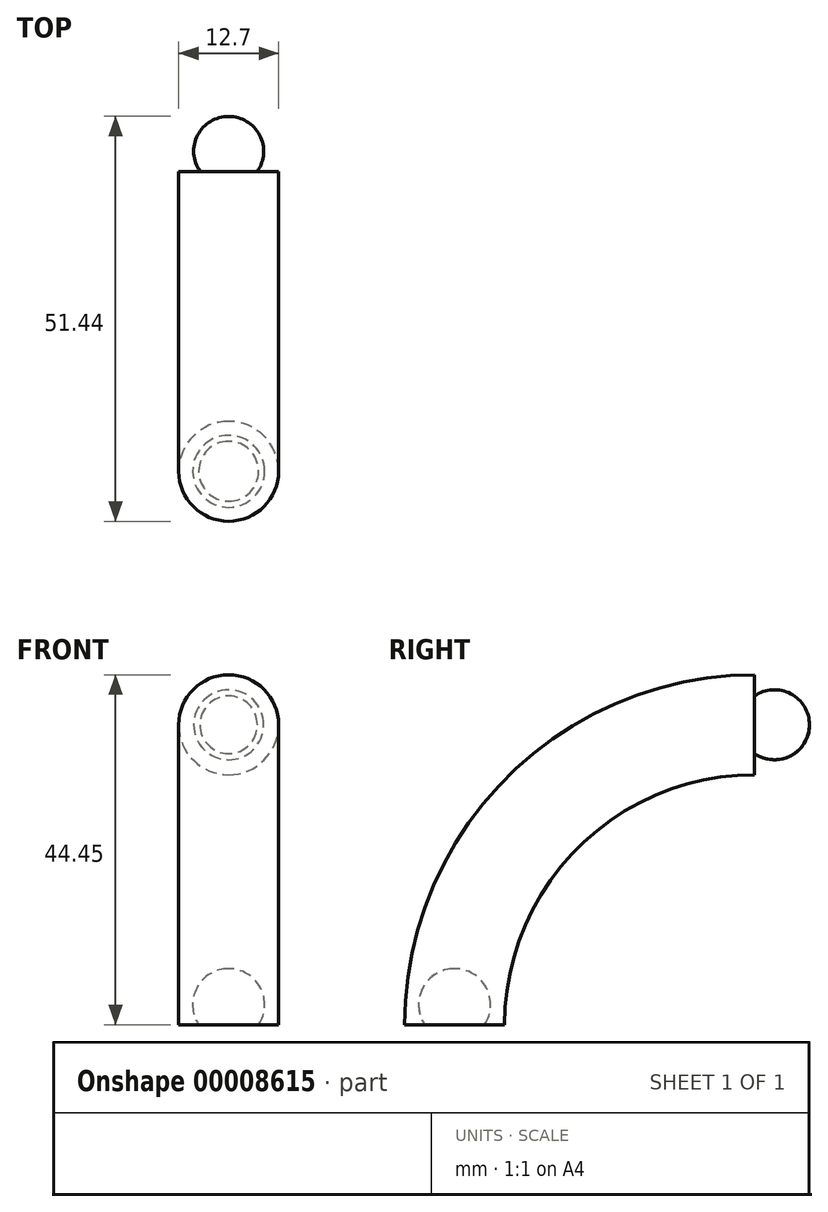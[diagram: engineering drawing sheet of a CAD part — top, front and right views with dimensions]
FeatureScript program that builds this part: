
annotation { "Feature Type Name" : "Feature", "Feature Type Description" : "" }
export const myFeature = defineFeature(function(context is Context, id is Id, definition is map)
    precondition{}
    {
        {
            var Q0;
            Q0=qCreatedBy(makeId("Front.planeOp"),FACE);
            var sketch = newSketch(context, id + "F0", { "sketchPlane" : qUnion([Q0])});
            skCircle(sketch, "E0", {"center": v(0, 38.1) * mm, "radius": 6.35 * mm});
            skLineSegment(sketch, "E1", {"start": v(-45.38, 0) * mm, "end": v(46.17, 0) * mm, "construction": true});
            skSolve(sketch);
        }
        {
            var Q0;
            Q0=makeQuery(id+"F0.imprint","IMPRINT",FACE,{"disambiguationData":[TD([[makeQuery(id+"F0.imprint","IMPRINT",EDGE,{"derivedFrom":sQuery(id+"F0.wireOp",EDGE,"E0")}),1.0]])]});
            var Q1;
            Q1=sQuery(id+"F0.wireOp",EDGE,"E1");
            revolve(context, id + "F1", {"entities" : qUnion([Q0]), "axis" : qUnion([Q1]), "revolveType" : RevolveType.ONE_DIRECTION, "angle" : 90 * degree});
        }
        {
            var Q0;
            Q0=qCreatedBy(makeId("Right.planeOp"),FACE);
            var sketch = newSketch(context, id + "F2", { "sketchPlane" : qUnion([Q0])});
            skLineSegment(sketch, "E2.0", {"start": v(0, 31.75) * mm, "end": v(0, 44.45) * mm, "construction": true});
            skLineSegment(sketch, "E3", {"start": v(0, 38.1) * mm, "end": v(16.92, 38.1) * mm, "construction": true});
            skArc(sketch, "E4", {"start": v(6.99, 38.1) * mm, "mid": v(2.54, 42.55) * mm, "end": v(-1.9, 38.1) * mm});
            skLineSegment(sketch, "E5", {"start": v(16.92, 38.1) * mm, "end": v(6.99, 38.1) * mm, "construction": true});
            skLineSegment(sketch, "E6", {"start": v(-1.9, 38.1) * mm, "end": v(-5.85, 38.1) * mm, "construction": true});
            skLineSegment(sketch, "E7", {"start": v(6.99, 38.1) * mm, "end": v(-1.9, 38.1) * mm, "construction": true});
            skLineSegment(sketch, "E8", {"start": v(-1.9, 38.1) * mm, "end": v(6.99, 38.1) * mm});
            skSolve(sketch);
        }
        {
            var Q0;
            Q0=makeQuery(id+"F2.imprint","IMPRINT",FACE,{"disambiguationData":[TD([[makeQuery(id+"F2.imprint","IMPRINT",EDGE,{"derivedFrom":sQuery(id+"F2.wireOp",EDGE,"E4")}),1.0]])]});
            var Q1;
            Q1=sQuery(id+"F2.wireOp",EDGE,"E5");
            revolve(context, id + "F3", {"operationType" : NewBodyOperationType.ADD, "entities" : qUnion([Q0]), "axis" : qUnion([Q1]), "revolveType" : RevolveType.FULL});
        }
        {
            var Q0;
            Q0=qCreatedBy(makeId("Right.planeOp"),FACE);
            var sketch = newSketch(context, id + "F4", { "sketchPlane" : qUnion([Q0])});
            skLineSegment(sketch, "E9.0", {"start": v(-31.75, 0) * mm, "end": v(-44.45, 0) * mm, "construction": true});
            skLineSegment(sketch, "E10", {"start": v(-38.1, 0) * mm, "end": v(-38.1, -14.63) * mm, "construction": true});
            skLineSegment(sketch, "E11", {"start": v(-38.1, -14.63) * mm, "end": v(-38.1, 5.3) * mm, "construction": true});
            skArc(sketch, "E12", {"start": v(-38.1, -2.03) * mm, "mid": v(-33.53, 2.54) * mm, "end": v(-38.1, 7.11) * mm});
            skPoint(sketch, "E13.center.orphan", {"position": v(-38.1, 3.81) * mm});
            skLineSegment(sketch, "E14", {"start": v(-38.1, 7.11) * mm, "end": v(-38.1, -2.03) * mm});
            skSolve(sketch);
        }
        {
            var Q0;
            Q0=makeQuery(id+"F4.imprint","IMPRINT",FACE,{"disambiguationData":[TD([[makeQuery(id+"F4.imprint","IMPRINT",EDGE,{"derivedFrom":sQuery(id+"F4.wireOp",EDGE,"E12")}),1.0]])]});
            var Q1;
            Q1=sQuery(id+"F4.wireOp",EDGE,"E11");
            revolve(context, id + "F5", {"entities" : qUnion([Q0]), "axis" : qUnion([Q1]), "revolveType" : RevolveType.FULL});
        }
        {
            var Q0;
            Q0=makeQuery(id+"F5.opRevolve","SWEPT_BODY",BODY,{"disambiguationData":[OSD([sQuery(id+"F4.wireOp",EDGE,"E12"),sQuery(id+"F4.wireOp",EDGE,"E14")])]});
            var Q1;
            Q1=makeQuery(id+"F1.opRevolve","SWEPT_BODY",BODY,{"disambiguationData":[OSD([sQuery(id+"F0.wireOp",EDGE,"E0")])]});
            var Q2;
            Q2=makeQuery(id+"F5.opRevolve","SWEPT_FACE",FACE,{"disambiguationData":[OSD([sQuery(id+"F4.wireOp",EDGE,"E12")])]});
            booleanBodies(context, id + "F6", {"operationType" : BooleanOperationType.SUBTRACTION, "tools" : qUnion([Q0]), "targets" : qUnion([Q1]), "entitiesToOffset" : qUnion([Q2])});
        }
    });
